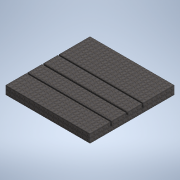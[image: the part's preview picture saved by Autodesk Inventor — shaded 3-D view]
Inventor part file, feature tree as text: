
AUTODESK INVENTOR PART (.ipt)
format: ipt  version: 2022 (Build 260153000, 153)  size: 197,120 bytes
history: native  units: in
note: dims shown in document units (in); Inventor stores cm internally (conversion verified against a paired STEP export)
features: extrude x3, sketch x3
ambient origin geometry x8: Origin, YZ Plane, XZ Plane, XY Plane, X Axis, Y Axis, Z Axis, Center Point
bodies: Solid1 (feature_tree)
feature tree (6):
  extrude  "Extrusion1"  Depth=157.4803in
  extrude  "Extrusion2"  Depth=15.748in TaperAngle=0.0deg
  extrude  "Extrusion3"  Depth=59.0551in
  sketch  "Sketch1"  dims[d1=157.4803in d2=157.4803in]
  sketch  "Sketch2"  dims[d3=157.4803in d4=15.748in d5=0.0in]
  sketch  "Sketch3"  dims[d6=39.3701in d7=59.0551in d8=1.1811in d9=3.5433in d10=0.3937in d11=5.315in d12=3.1496in d13=0.3937in d14=0.3937in d15=0.315in d16=1.5748in d17=0.1969in d18=0.1969in d19=0.1969in d20=1.1811in d21=2.3622in d22=3.5433in d23=0.3937in d24=5.315in d25=0.3937in d26=0.315in d27=1.5748in d28=0.1969in d29=0.1969in d30=0.3937in d31=157.4803in d32=0.0in d33=68.8976in d34=1.2795in d35=2.5591in d36=1.7717in d37=1.1811in d38=4.1339in d39=4.9213in d40=1.1811in d41=157.4803in d42=0.0in]
